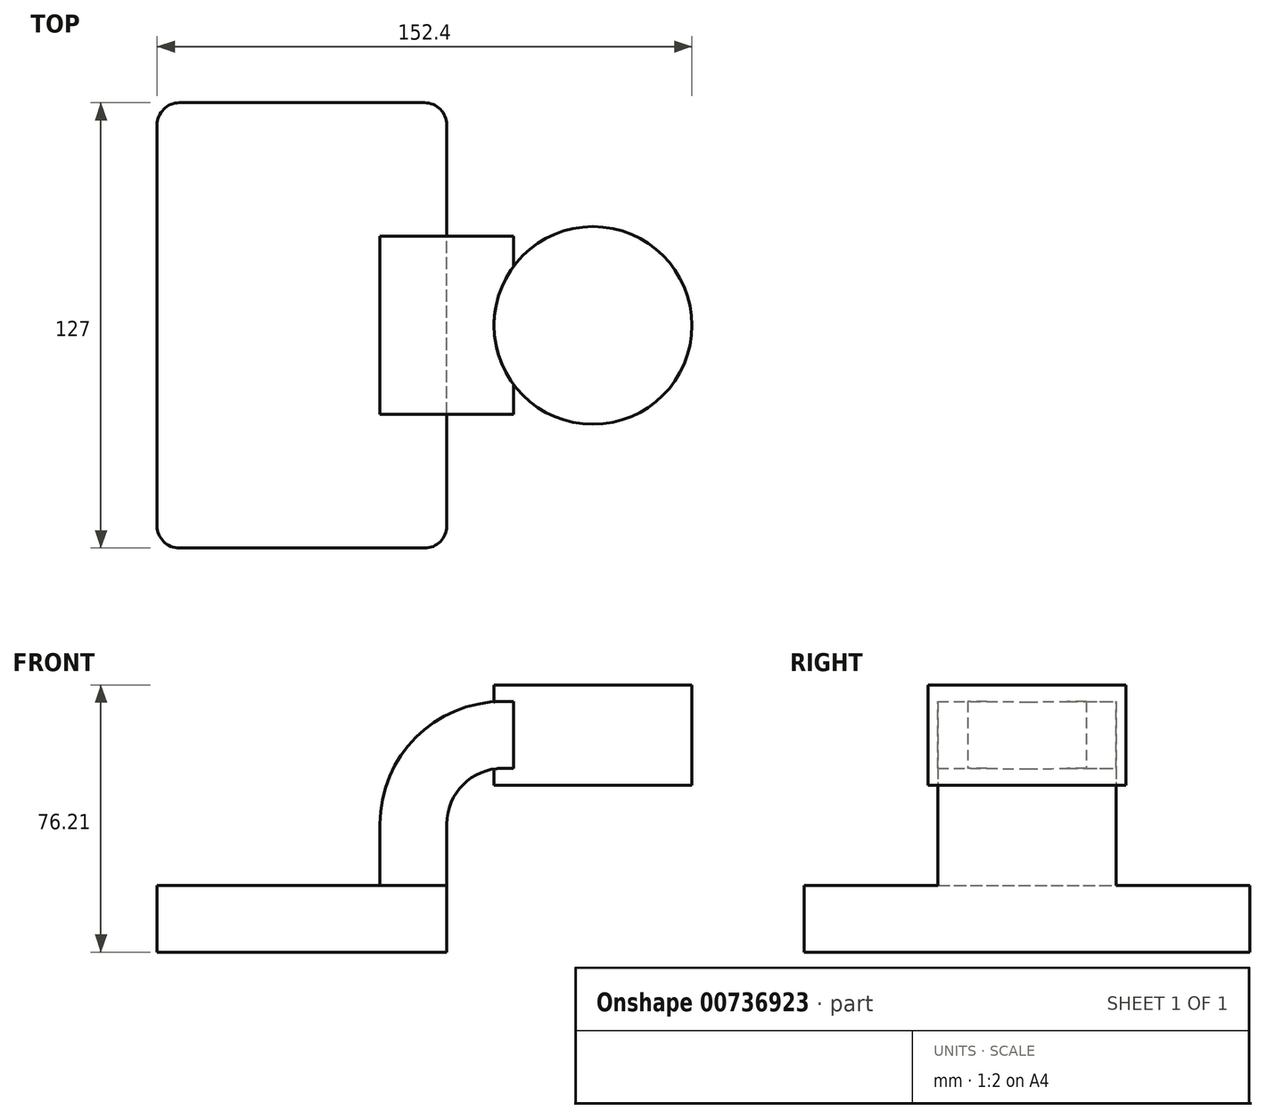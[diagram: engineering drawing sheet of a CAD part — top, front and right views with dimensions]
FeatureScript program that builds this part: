
annotation { "Feature Type Name" : "Feature", "Feature Type Description" : "" }
export const myFeature = defineFeature(function(context is Context, id is Id, definition is map)
    precondition{}
    {
        {
            var Q0;
            Q0=qCreatedBy(makeId("Front.planeOp"),FACE);
            var sketch = newSketch(context, id + "F0", { "sketchPlane" : qUnion([Q0])});
            skLineSegment(sketch, "E0.bottom", {"start": v(41.27, 9.53) * mm, "end": v(-41.28, 9.53) * mm});
            skLineSegment(sketch, "E0.top", {"start": v(41.28, -9.52) * mm, "end": v(-41.27, -9.52) * mm});
            skLineSegment(sketch, "E0.left", {"start": v(41.28, 9.53) * mm, "end": v(41.28, -9.52) * mm});
            skLineSegment(sketch, "E0.right", {"start": v(-41.28, 9.53) * mm, "end": v(-41.27, -9.52) * mm});
            skPoint(sketch, "E0.middle", {"position": v(0, 0) * mm});
            skLineSegment(sketch, "E1.bottom", {"start": v(111.13, 38.1) * mm, "end": v(60.32, 38.1) * mm});
            skLineSegment(sketch, "E1.top", {"start": v(111.12, 66.68) * mm, "end": v(60.32, 66.68) * mm});
            skLineSegment(sketch, "E1.left", {"start": v(111.12, 38.1) * mm, "end": v(111.12, 66.68) * mm});
            skLineSegment(sketch, "E1.right", {"start": v(60.32, 38.1) * mm, "end": v(60.32, 66.68) * mm});
            skPoint(sketch, "E1.middle", {"position": v(85.72, 52.39) * mm});
            skLineSegment(sketch, "E2", {"start": v(41.27, 9.53) * mm, "end": v(41.27, 27) * mm});
            skArc(sketch, "E3", {"start": v(41.27, 27) * mm, "mid": v(45.92, 38.23) * mm, "end": v(57.15, 42.88) * mm});
            skLineSegment(sketch, "E4", {"start": v(57.15, 42.88) * mm, "end": v(82.93, 42.88) * mm});
            skLineSegment(sketch, "E5.0", {"start": v(57.15, 61.93) * mm, "end": v(82.93, 61.93) * mm});
            skArc(sketch, "E5.1", {"start": v(22.23, 27) * mm, "mid": v(32.45, 51.7) * mm, "end": v(57.15, 61.93) * mm});
            skLineSegment(sketch, "E5.2", {"start": v(22.23, 9.53) * mm, "end": v(22.23, 27) * mm});
            skLineSegment(sketch, "E6", {"start": v(82.93, 38.1) * mm, "end": v(82.93, 66.68) * mm});
            skFitSpline(sketch, "E7", {"points": [v(-41.28, 9.53) * mm, v(57.15, 61.93) * mm], "startDerivative": vector(-2.58, 90.31) * mm, "endDerivative": vector(105.02, -2.62) * mm});
            skSolve(sketch);
        }
        {
            var Q0;
            Q0=makeQuery(id+"F0.imprint","IMPRINT",FACE,{"disambiguationData":[TD([[makeQuery(id+"F0.imprint","IMPRINT",EDGE,{"derivedFrom":sQuery(id+"F0.wireOp",EDGE,"E0.top")}),-1.0]])]});
            extrude(context, id + "F1", {"entities" : qUnion([Q0]), "endBound" : BoundingType.SYMMETRIC, "depth" : 127 * mm, "offsetDistance" : 25.4 * mm});
        }
        {
            var Q0;
            {var subQ1=sQuery(id+"F0.wireOp",EDGE,"E2");Q0=makeQuery(id+"F0.imprint","IMPRINT",FACE,{"disambiguationData":[TD([[makeQuery(id+"F0.imprint","IMPRINT",EDGE,{"derivedFrom":subQ1}),1.0]])]});}
            extrude(context, id + "F2", {"entities" : qUnion([Q0]), "operationType" : NewBodyOperationType.ADD, "endBound" : BoundingType.SYMMETRIC, "depth" : 50.8 * mm, "offsetDistance" : 25.4 * mm});
        }
        {
            var Q0;
            Q0=makeQuery(id+"F0.imprint","IMPRINT",FACE,{"disambiguationData":[TD([[makeQuery(id+"F0.imprint","IMPRINT",EDGE,{"derivedFrom":sQuery(id+"F0.wireOp",EDGE,"E5.1")}),1.0]])]});
            extrude(context, id + "F3", {"entities" : qUnion([Q0]), "operationType" : NewBodyOperationType.ADD, "endBound" : BoundingType.SYMMETRIC, "depth" : 15.88 * mm, "offsetDistance" : 25.4 * mm});
        }
        {
            var Q0;
            {var subQ4=sQuery(id+"F0.wireOp",EDGE,"E1.left");Q0=makeQuery(id+"F0.imprint","IMPRINT",FACE,{"disambiguationData":[TD([[makeQuery(id+"F0.imprint","IMPRINT",EDGE,{"derivedFrom":subQ4}),1.0]])]});}
            var Q1;
            Q1=sQuery(id+"F0.wireOp",EDGE,"E6");
            revolve(context, id + "F4", {"operationType" : NewBodyOperationType.ADD, "surfaceOperationType" : NewSurfaceOperationType.NEW, "entities" : qUnion([Q0]), "axis" : qUnion([Q1]), "revolveType" : RevolveType.FULL});
        }
        {
            var Q0;
            Q0=makeQuery(id+"F1.opExtrude","CAP_EDGE",EDGE,{"disambiguationData":[OSD([sQuery(id+"F0.wireOp",EDGE,"E0.left")])],"isStart":false});
            var Q1;
            Q1=makeQuery(id+"F1.opExtrude","CAP_EDGE",EDGE,{"disambiguationData":[OSD([sQuery(id+"F0.wireOp",EDGE,"E0.right")])],"isStart":false});
            var Q2;
            Q2=makeQuery(id+"F1.opExtrude","CAP_EDGE",EDGE,{"disambiguationData":[OSD([sQuery(id+"F0.wireOp",EDGE,"E0.left")])],"isStart":true});
            var Q3;
            Q3=makeQuery(id+"F1.opExtrude","CAP_EDGE",EDGE,{"disambiguationData":[OSD([sQuery(id+"F0.wireOp",EDGE,"E0.right")])],"isStart":true});
            fillet(context, id + "F5", {"entities" : qUnion([Q0, Q1, Q2, Q3]), "radius" : 6.35 * mm, "tangentPropagation" : true, "allowEdgeOverflow" : false});
        }
    });
